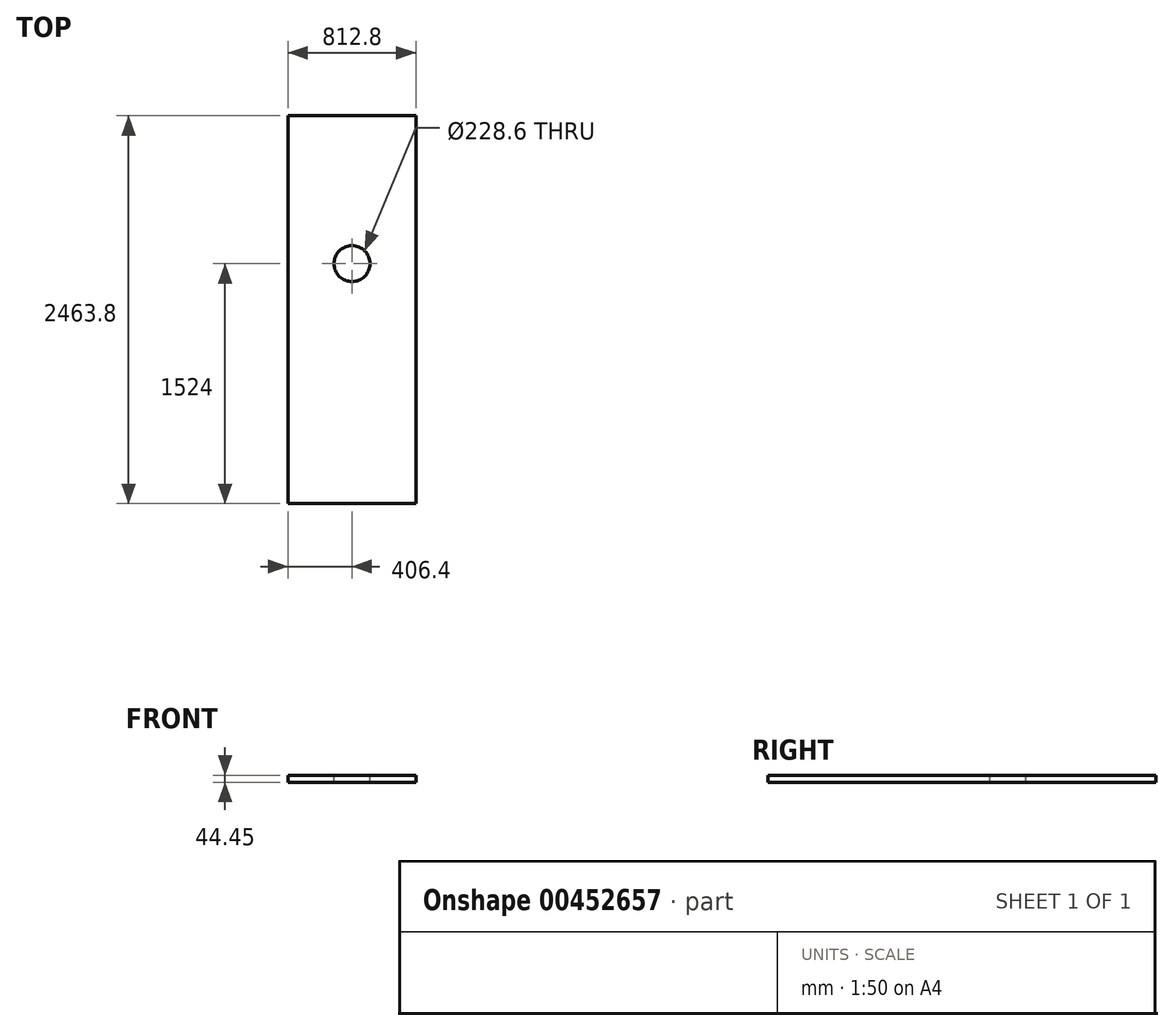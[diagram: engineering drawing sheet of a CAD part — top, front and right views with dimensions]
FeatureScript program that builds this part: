
annotation { "Feature Type Name" : "Feature", "Feature Type Description" : "" }
export const myFeature = defineFeature(function(context is Context, id is Id, definition is map)
    precondition{}
    {
        {
            var Q0;
            Q0=qCreatedBy(makeId("Top.planeOp"),FACE);
            var sketch = newSketch(context, id + "F0", { "sketchPlane" : qUnion([Q0])});
            skLineSegment(sketch, "E0", {"start": v(0, 0) * mm, "end": v(0, 2463.8) * mm});
            skLineSegment(sketch, "E1", {"start": v(0, 2463.8) * mm, "end": v(812.8, 2463.8) * mm});
            skPoint(sketch, "E2.endSnap0", {"position": v(406.4, 2463.8) * mm});
            skLineSegment(sketch, "E3", {"start": v(812.8, 2463.8) * mm, "end": v(812.8, 0) * mm});
            skLineSegment(sketch, "E4", {"start": v(0, 0) * mm, "end": v(812.8, 0) * mm});
            skSolve(sketch);
        }
        {
            var Q0;
            Q0=makeQuery(id+"F0.imprint","IMPRINT",FACE,{"disambiguationData":[TD([[makeQuery(id+"F0.imprint","IMPRINT",EDGE,{"derivedFrom":sQuery(id+"F0.wireOp",EDGE,"E0")}),-1.0]])]});
            var Q1;
            Q1 = qSketchRegion(id + "F2", true);
            extrude(context, id + "F1", {"entities" : qUnion([Q0, Q1]), "depth" : 44.45 * mm});
        }
        {
            var Q0;
            Q0=makeQuery(id+"F1.opExtrude","CAP_FACE",FACE,{"disambiguationData":[OSD([sQuery(id+"F0.wireOp",EDGE,"E0"),sQuery(id+"F0.wireOp",EDGE,"E1"),sQuery(id+"F0.wireOp",EDGE,"E3"),sQuery(id+"F0.wireOp",EDGE,"E4")])],"isStart":false});
            var sketch = newSketch(context, id + "F2", { "sketchPlane" : qUnion([Q0])});
            skCircle(sketch, "E5", {"center": v(406.4, 1524) * mm, "radius": 114.3 * mm});
            skSolve(sketch);
        }
        {
            var Q0;
            Q0=sQuery(id+"F2.wireOp",VERTEX,"E5.center");
            var Q1;
            Q1=makeQuery(id+"F1.opExtrude","SWEPT_BODY",BODY,{"disambiguationData":[OSD([sQuery(id+"F0.wireOp",EDGE,"E0"),sQuery(id+"F0.wireOp",EDGE,"E1"),sQuery(id+"F0.wireOp",EDGE,"E3"),sQuery(id+"F0.wireOp",EDGE,"E4")])]});
            hole(context, id + "F3", {"style" : HoleStyle.SIMPLE, "endStyle" : HoleEndStyle.THROUGH, "holeDiameter" : 228.6 * mm, "isTappedThrough" : true, "tappedDepth" : 12.7 * mm, "tapClearance" : 3, "locations" : qUnion([Q0]), "scope" : qUnion([Q1])});
        }
        {
            var Q0;
            Q0=makeQuery(id+"F1.opExtrude","CAP_FACE",FACE,{"disambiguationData":[OSD([sQuery(id+"F0.wireOp",EDGE,"E0"),sQuery(id+"F0.wireOp",EDGE,"E1"),sQuery(id+"F0.wireOp",EDGE,"E3"),sQuery(id+"F0.wireOp",EDGE,"E4")])],"isStart":false});
            var sketch = newSketch(context, id + "F4", { "sketchPlane" : qUnion([Q0])});
            skLineSegment(sketch, "E6", {"start": v(0, 177.8) * mm, "end": v(812.8, 177.8) * mm});
            skLineSegment(sketch, "E7", {"start": v(812.8, 228.6) * mm, "end": v(0, 228.6) * mm});
            skLineSegment(sketch, "E8", {"start": v(812.8, 279.4) * mm, "end": v(0, 279.4) * mm});
            skLineSegment(sketch, "E9", {"start": v(0, 279.4) * mm, "end": v(0, 330.2) * mm});
            skLineSegment(sketch, "E10", {"start": v(0, 330.2) * mm, "end": v(812.8, 330.2) * mm});
            skLineSegment(sketch, "E11", {"start": v(812.8, 330.2) * mm, "end": v(812.8, 381) * mm});
            skLineSegment(sketch, "E12", {"start": v(812.8, 381) * mm, "end": v(0, 381) * mm});
            skLineSegment(sketch, "E13", {"start": v(0, 381) * mm, "end": v(0, 431.8) * mm});
            skLineSegment(sketch, "E14", {"start": v(0, 431.8) * mm, "end": v(812.8, 431.8) * mm});
            skLineSegment(sketch, "E15", {"start": v(812.8, 431.8) * mm, "end": v(812.8, 482.6) * mm});
            skLineSegment(sketch, "E16", {"start": v(812.8, 482.6) * mm, "end": v(0, 482.6) * mm});
            skLineSegment(sketch, "E17", {"start": v(0, 482.6) * mm, "end": v(0, 533.4) * mm});
            skLineSegment(sketch, "E18", {"start": v(0, 533.4) * mm, "end": v(812.8, 533.4) * mm});
            skLineSegment(sketch, "E19", {"start": v(812.8, 533.4) * mm, "end": v(812.8, 584.2) * mm});
            skLineSegment(sketch, "E20", {"start": v(812.8, 584.2) * mm, "end": v(0, 584.2) * mm});
            skLineSegment(sketch, "E21", {"start": v(0, 584.2) * mm, "end": v(0, 635) * mm});
            skLineSegment(sketch, "E22", {"start": v(0, 635) * mm, "end": v(812.8, 635) * mm});
            skLineSegment(sketch, "E23", {"start": v(812.8, 685.8) * mm, "end": v(0, 685.8) * mm});
            skLineSegment(sketch, "E24", {"start": v(0, 685.8) * mm, "end": v(0, 736.6) * mm});
            skLineSegment(sketch, "E25", {"start": v(0, 736.6) * mm, "end": v(812.8, 736.6) * mm});
            skLineSegment(sketch, "E26", {"start": v(812.8, 736.6) * mm, "end": v(812.8, 787.4) * mm});
            skLineSegment(sketch, "E27", {"start": v(812.8, 787.4) * mm, "end": v(0, 787.4) * mm});
            skLineSegment(sketch, "E28", {"start": v(0, 787.4) * mm, "end": v(0, 838.2) * mm});
            skLineSegment(sketch, "E29", {"start": v(0, 838.2) * mm, "end": v(812.8, 838.2) * mm});
            skLineSegment(sketch, "E30", {"start": v(812.8, 838.2) * mm, "end": v(812.8, 889) * mm});
            skLineSegment(sketch, "E31", {"start": v(812.8, 889) * mm, "end": v(0, 889) * mm});
            skLineSegment(sketch, "E32", {"start": v(0, 889) * mm, "end": v(0, 939.8) * mm});
            skLineSegment(sketch, "E33", {"start": v(0, 939.8) * mm, "end": v(812.8, 939.8) * mm});
            skLineSegment(sketch, "E34", {"start": v(812.8, 939.8) * mm, "end": v(812.8, 990.6) * mm});
            skLineSegment(sketch, "E35", {"start": v(812.8, 990.6) * mm, "end": v(0, 990.6) * mm});
            skLineSegment(sketch, "E36", {"start": v(0, 990.6) * mm, "end": v(0, 1041.4) * mm});
            skLineSegment(sketch, "E37", {"start": v(0, 1041.4) * mm, "end": v(812.8, 1041.4) * mm});
            skLineSegment(sketch, "E38", {"start": v(812.8, 1041.4) * mm, "end": v(812.8, 1092.2) * mm});
            skLineSegment(sketch, "E39", {"start": v(812.8, 1092.2) * mm, "end": v(0, 1092.2) * mm});
            skLineSegment(sketch, "E40", {"start": v(0, 1092.2) * mm, "end": v(0, 1143) * mm});
            skLineSegment(sketch, "E41", {"start": v(0, 1143) * mm, "end": v(812.8, 1143) * mm});
            skLineSegment(sketch, "E42", {"start": v(812.8, 1143) * mm, "end": v(812.8, 1231.9) * mm});
            skLineSegment(sketch, "E43", {"start": v(0, 1231.9) * mm, "end": v(0, 1244.6) * mm});
            skLineSegment(sketch, "E44", {"start": v(0, 1244.6) * mm, "end": v(812.8, 1244.6) * mm});
            skLineSegment(sketch, "E45", {"start": v(812.8, 1244.6) * mm, "end": v(812.8, 1295.4) * mm});
            skLineSegment(sketch, "E46", {"start": v(812.8, 1295.4) * mm, "end": v(0, 1295.4) * mm});
            skLineSegment(sketch, "E47", {"start": v(0, 1295.4) * mm, "end": v(0, 1346.2) * mm});
            skLineSegment(sketch, "E48", {"start": v(0, 1346.2) * mm, "end": v(812.8, 1346.2) * mm});
            skLineSegment(sketch, "E49", {"start": v(812.8, 1346.2) * mm, "end": v(812.8, 1397) * mm});
            skLineSegment(sketch, "E50", {"start": v(812.8, 1397) * mm, "end": v(490.64, 1397) * mm});
            skLineSegment(sketch, "E51", {"start": v(0, 1397) * mm, "end": v(0, 1447.8) * mm});
            skLineSegment(sketch, "E52", {"start": v(0, 1447.8) * mm, "end": v(274.42, 1447.8) * mm});
            skLineSegment(sketch, "E53", {"start": v(812.8, 1447.8) * mm, "end": v(812.8, 1498.6) * mm});
            skLineSegment(sketch, "E54", {"start": v(812.8, 1498.6) * mm, "end": v(556.67, 1498.6) * mm});
            skLineSegment(sketch, "E55", {"start": v(0, 1498.6) * mm, "end": v(0, 1549.4) * mm});
            skLineSegment(sketch, "E56", {"start": v(0, 1549.4) * mm, "end": v(256.13, 1549.4) * mm});
            skLineSegment(sketch, "E57", {"start": v(812.8, 1549.4) * mm, "end": v(812.8, 1600.2) * mm});
            skLineSegment(sketch, "E58", {"start": v(812.8, 1600.2) * mm, "end": v(538.38, 1600.2) * mm});
            skLineSegment(sketch, "E59", {"start": v(0, 1600.2) * mm, "end": v(0, 1651) * mm});
            skLineSegment(sketch, "E60", {"start": v(0, 1651) * mm, "end": v(322.16, 1651) * mm});
            skLineSegment(sketch, "E61", {"start": v(812.8, 1651) * mm, "end": v(812.8, 1701.8) * mm});
            skLineSegment(sketch, "E62", {"start": v(812.8, 1701.8) * mm, "end": v(0, 1701.8) * mm});
            skLineSegment(sketch, "E63", {"start": v(0, 1701.8) * mm, "end": v(0, 1752.6) * mm});
            skLineSegment(sketch, "E64", {"start": v(0, 1752.6) * mm, "end": v(812.8, 1752.6) * mm});
            skLineSegment(sketch, "E65", {"start": v(812.8, 1752.6) * mm, "end": v(812.8, 1803.4) * mm});
            skLineSegment(sketch, "E66", {"start": v(812.8, 1803.4) * mm, "end": v(0, 1803.4) * mm});
            skLineSegment(sketch, "E67", {"start": v(0, 1803.4) * mm, "end": v(0, 1854.2) * mm});
            skLineSegment(sketch, "E68", {"start": v(0, 1854.2) * mm, "end": v(812.8, 1854.2) * mm});
            skLineSegment(sketch, "E69", {"start": v(812.8, 1854.2) * mm, "end": v(812.8, 1905) * mm});
            skLineSegment(sketch, "E70", {"start": v(812.8, 1905) * mm, "end": v(0, 1905) * mm});
            skLineSegment(sketch, "E71", {"start": v(0, 1193.8) * mm, "end": v(812.8, 1193.8) * mm});
            skLineSegment(sketch, "E72", {"start": v(0, 2159) * mm, "end": v(812.8, 2159) * mm});
            skLineSegment(sketch, "E73", {"start": v(812.8, 1955.8) * mm, "end": v(0, 1955.8) * mm});
            skLineSegment(sketch, "E74", {"start": v(0, 1955.8) * mm, "end": v(0, 2006.6) * mm});
            skLineSegment(sketch, "E75", {"start": v(0, 2006.6) * mm, "end": v(812.8, 2006.6) * mm});
            skLineSegment(sketch, "E76", {"start": v(812.8, 2006.6) * mm, "end": v(812.8, 2057.4) * mm});
            skLineSegment(sketch, "E77", {"start": v(812.8, 2057.4) * mm, "end": v(0, 2057.4) * mm});
            skLineSegment(sketch, "E78", {"start": v(0, 2057.4) * mm, "end": v(0, 2108.2) * mm});
            skLineSegment(sketch, "E79", {"start": v(0, 2108.2) * mm, "end": v(812.8, 2108.2) * mm});
            skLineSegment(sketch, "E80", {"start": v(517.28, 1549.4) * mm, "end": v(517.84, 1549.4) * mm});
            skLineSegment(sketch, "E81", {"start": v(321.46, 1600.2) * mm, "end": v(321.2, 1600.2) * mm});
            skCircle(sketch, "E82", {"center": v(406.4, 1524) * mm, "radius": 114.3 * mm});
            skLineSegment(sketch, "E83.trimOffspring", {"start": v(256.13, 1498.6) * mm, "end": v(0, 1498.6) * mm});
            skLineSegment(sketch, "E84.trimOffspring", {"start": v(538.38, 1447.8) * mm, "end": v(812.8, 1447.8) * mm});
            skCircle(sketch, "E85", {"center": v(406.4, 1524) * mm, "radius": 152.4 * mm});
            skLineSegment(sketch, "E86.trimOffspring", {"start": v(322.16, 1397) * mm, "end": v(0, 1397) * mm});
            skLineSegment(sketch, "E87.trimOffspring", {"start": v(294.96, 1549.4) * mm, "end": v(295.3, 1549.4) * mm});
            skLineSegment(sketch, "E88.trimOffspring", {"start": v(274.42, 1600.2) * mm, "end": v(0, 1600.2) * mm});
            skLineSegment(sketch, "E89.trimOffspring", {"start": v(490.64, 1651) * mm, "end": v(812.8, 1651) * mm});
            skLineSegment(sketch, "E90.trimOffspring", {"start": v(491.6, 1600.2) * mm, "end": v(490.49, 1600.2) * mm});
            skLineSegment(sketch, "E91.trimOffspring", {"start": v(556.67, 1549.4) * mm, "end": v(812.8, 1549.4) * mm});
            skSolve(sketch);
        }
        {
            var Q0;
            {var subQ0=sQuery(id+"F4.wireOp",EDGE,"E72");Q0=makeQuery(id+"F4.imprint","IMPRINT",FACE,{"disambiguationData":[TD([[makeQuery(id+"F4.imprint","IMPRINT",EDGE,{"derivedFrom":subQ0}),-1.0]])]});}
            var Q1;
            {var subQ0=sQuery(id+"F4.wireOp",EDGE,"E75");Q1=makeQuery(id+"F4.imprint","IMPRINT",FACE,{"disambiguationData":[TD([[makeQuery(id+"F4.imprint","IMPRINT",EDGE,{"derivedFrom":subQ0}),1.0]])]});}
            var Q2;
            {var subQ0=sQuery(id+"F4.wireOp",EDGE,"E70");Q2=makeQuery(id+"F4.imprint","IMPRINT",FACE,{"disambiguationData":[TD([[makeQuery(id+"F4.imprint","IMPRINT",EDGE,{"derivedFrom":subQ0}),-1.0]])]});}
            var Q3;
            {var subQ0=sQuery(id+"F4.wireOp",EDGE,"E66");Q3=makeQuery(id+"F4.imprint","IMPRINT",FACE,{"disambiguationData":[TD([[makeQuery(id+"F4.imprint","IMPRINT",EDGE,{"derivedFrom":subQ0}),-1.0]])]});}
            var Q4;
            {var subQ0=sQuery(id+"F4.wireOp",EDGE,"E62");Q4=makeQuery(id+"F4.imprint","IMPRINT",FACE,{"disambiguationData":[TD([[makeQuery(id+"F4.imprint","IMPRINT",EDGE,{"derivedFrom":subQ0}),-1.0]])]});}
            var Q5;
            {var subQ0=sQuery(id+"F4.wireOp",EDGE,"E55");Q5=makeQuery(id+"F4.imprint","IMPRINT",FACE,{"disambiguationData":[TD([[makeQuery(id+"F4.imprint","IMPRINT",EDGE,{"derivedFrom":subQ0}),-1.0]])]});}
            var Q6;
            {var subQ0=sQuery(id+"F4.wireOp",EDGE,"E54");Q6=makeQuery(id+"F4.imprint","IMPRINT",FACE,{"disambiguationData":[TD([[makeQuery(id+"F4.imprint","IMPRINT",EDGE,{"derivedFrom":subQ0}),-1.0]])]});}
            var Q7;
            {var subQ3=sQuery(id+"F4.wireOp",EDGE,"E50");Q7=makeQuery(id+"F4.imprint","IMPRINT",FACE,{"disambiguationData":[TD([[makeQuery(id+"F4.imprint","IMPRINT",EDGE,{"derivedFrom":subQ3}),-1.0]])]});}
            var Q8;
            {var subQ0=sQuery(id+"F4.wireOp",EDGE,"E46");Q8=makeQuery(id+"F4.imprint","IMPRINT",FACE,{"disambiguationData":[TD([[makeQuery(id+"F4.imprint","IMPRINT",EDGE,{"derivedFrom":subQ0}),-1.0]])]});}
            var Q9;
            {var subQ4=sQuery(id+"F4.wireOp",EDGE,"E43");Q9=makeQuery(id+"F4.imprint","IMPRINT",FACE,{"disambiguationData":[TD([[makeQuery(id+"F4.imprint","IMPRINT",EDGE,{"derivedFrom":subQ4}),-1.0]])]});}
            var Q10;
            {var subQ0=sQuery(id+"F4.wireOp",EDGE,"E39");Q10=makeQuery(id+"F4.imprint","IMPRINT",FACE,{"disambiguationData":[TD([[makeQuery(id+"F4.imprint","IMPRINT",EDGE,{"derivedFrom":subQ0}),-1.0]])]});}
            var Q11;
            {var subQ0=sQuery(id+"F4.wireOp",EDGE,"E35");Q11=makeQuery(id+"F4.imprint","IMPRINT",FACE,{"disambiguationData":[TD([[makeQuery(id+"F4.imprint","IMPRINT",EDGE,{"derivedFrom":subQ0}),-1.0]])]});}
            var Q12;
            {var subQ0=sQuery(id+"F4.wireOp",EDGE,"E31");Q12=makeQuery(id+"F4.imprint","IMPRINT",FACE,{"disambiguationData":[TD([[makeQuery(id+"F4.imprint","IMPRINT",EDGE,{"derivedFrom":subQ0}),-1.0]])]});}
            var Q13;
            {var subQ0=sQuery(id+"F4.wireOp",EDGE,"E27");Q13=makeQuery(id+"F4.imprint","IMPRINT",FACE,{"disambiguationData":[TD([[makeQuery(id+"F4.imprint","IMPRINT",EDGE,{"derivedFrom":subQ0}),-1.0]])]});}
            var Q14;
            {var subQ0=sQuery(id+"F4.wireOp",EDGE,"E23");Q14=makeQuery(id+"F4.imprint","IMPRINT",FACE,{"disambiguationData":[TD([[makeQuery(id+"F4.imprint","IMPRINT",EDGE,{"derivedFrom":subQ0}),-1.0]])]});}
            var Q15;
            {var subQ0=sQuery(id+"F4.wireOp",EDGE,"E20");Q15=makeQuery(id+"F4.imprint","IMPRINT",FACE,{"disambiguationData":[TD([[makeQuery(id+"F4.imprint","IMPRINT",EDGE,{"derivedFrom":subQ0}),-1.0]])]});}
            var Q16;
            {var subQ0=sQuery(id+"F4.wireOp",EDGE,"E16");Q16=makeQuery(id+"F4.imprint","IMPRINT",FACE,{"disambiguationData":[TD([[makeQuery(id+"F4.imprint","IMPRINT",EDGE,{"derivedFrom":subQ0}),-1.0]])]});}
            var Q17;
            {var subQ0=sQuery(id+"F4.wireOp",EDGE,"E12");Q17=makeQuery(id+"F4.imprint","IMPRINT",FACE,{"disambiguationData":[TD([[makeQuery(id+"F4.imprint","IMPRINT",EDGE,{"derivedFrom":subQ0}),-1.0]])]});}
            var Q18;
            {var subQ0=sQuery(id+"F4.wireOp",EDGE,"E8");Q18=makeQuery(id+"F4.imprint","IMPRINT",FACE,{"disambiguationData":[TD([[makeQuery(id+"F4.imprint","IMPRINT",EDGE,{"derivedFrom":subQ0}),-1.0]])]});}
            var Q19;
            {var subQ0=sQuery(id+"F4.wireOp",EDGE,"E6");Q19=makeQuery(id+"F4.imprint","IMPRINT",FACE,{"disambiguationData":[TD([[makeQuery(id+"F4.imprint","IMPRINT",EDGE,{"derivedFrom":subQ0}),1.0]])]});}
            var Q20;
            {var subQ0=sQuery(id+"F4.wireOp",EDGE,"E58");Q20=makeQuery(id+"F4.imprint","IMPRINT",FACE,{"disambiguationData":[TD([[makeQuery(id+"F4.imprint","IMPRINT",EDGE,{"derivedFrom":subQ0}),-1.0]])]});}
            var Q21;
            Q21=makeQuery(id+"F4.imprint","IMPRINT",FACE,{"disambiguationData":[TD([[makeQuery(id+"F4.imprint","IMPRINT",EDGE,{"derivedFrom":sQuery(id+"F4.wireOp",EDGE,"E51")}),-1.0]])]});
            var Q22;
            {var subQ8=sQuery(id+"F4.wireOp",EDGE,"E82");var subQ9=makeQuery(id+"F4.imprint","IMPRINT",VERTEX,{"disambiguationData":[OD(0.0)],"derivedFrom":subQ8});Q22=makeQuery(id+"F4.imprint","IMPRINT",FACE,{"disambiguationData":[TD([[makeQuery(id+"F4.imprint","IMPRINT",EDGE,{"disambiguationData":[TD([[subQ9,-1.0]])],"derivedFrom":subQ8}),-1.0]])]});}
            var Q23;
            Q23=makeQuery(id+"F4.imprint","IMPRINT",FACE,{"disambiguationData":[TD([[makeQuery(id+"F4.imprint","IMPRINT",EDGE,{"derivedFrom":sQuery(id+"F4.wireOp",EDGE,"E59")}),-1.0]])]});
            extrude(context, id + "F5", {"entities" : qUnion([Q0, Q1, Q2, Q3, Q4, Q5, Q6, Q7, Q8, Q9, Q10, Q11, Q12, Q13, Q14, Q15, Q16, Q17, Q18, Q19, Q20, Q21, Q22, Q23]), "operationType" : NewBodyOperationType.ADD, "depth" : -3.43 * mm});
        }
    });
